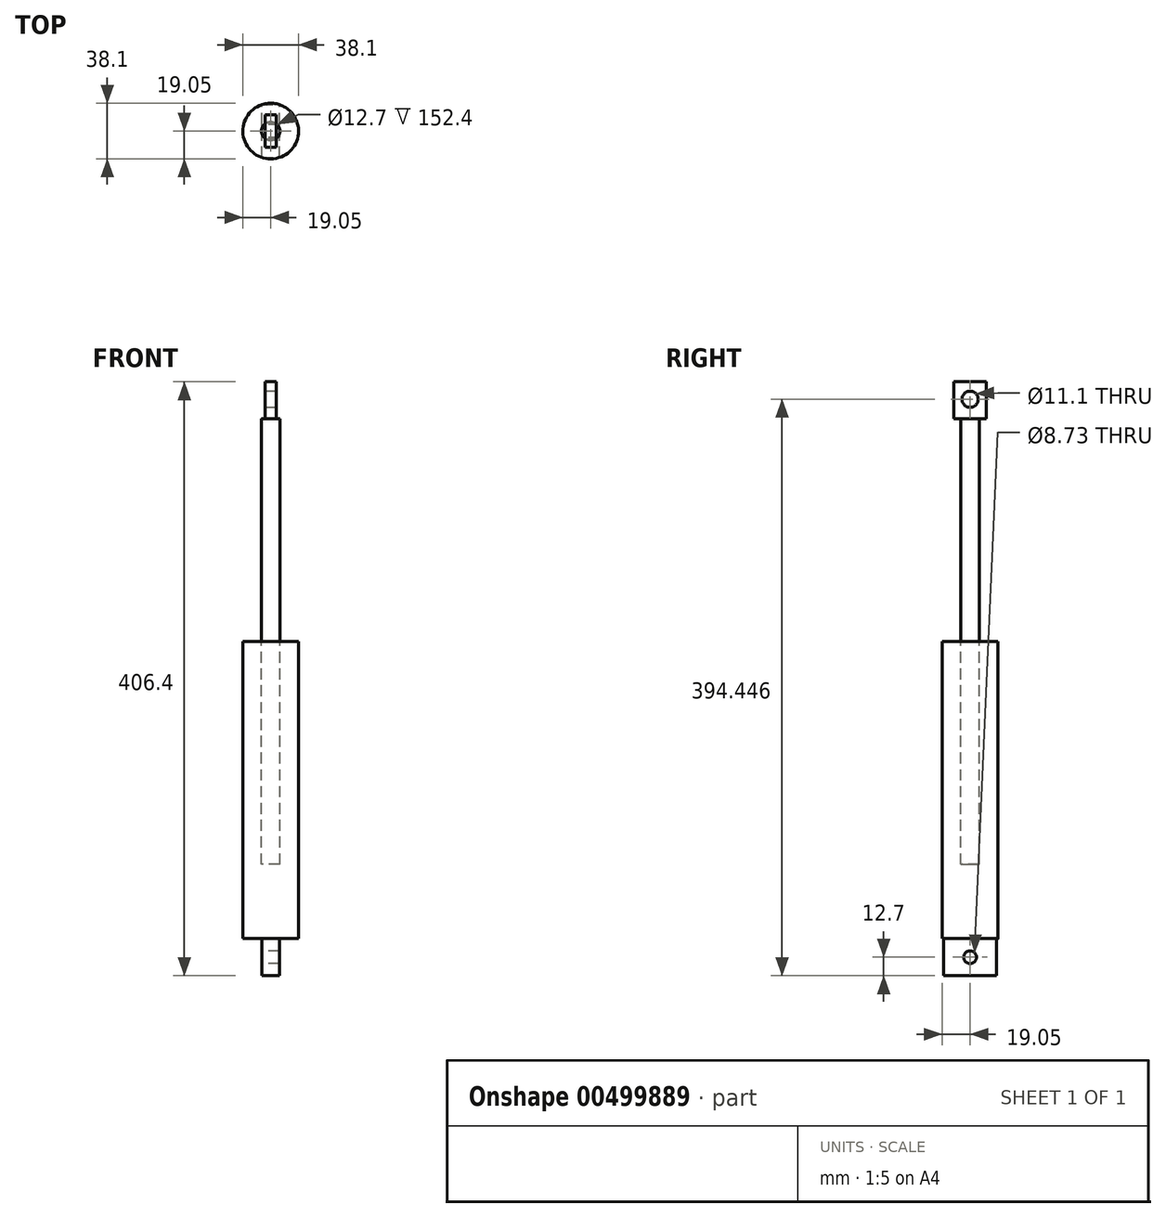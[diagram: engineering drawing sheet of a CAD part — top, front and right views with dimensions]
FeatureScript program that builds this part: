
annotation { "Feature Type Name" : "Feature", "Feature Type Description" : "" }
export const myFeature = defineFeature(function(context is Context, id is Id, definition is map)
    precondition{}
    {
        {
            var Q0;
            Q0=qCreatedBy(makeId("Top.planeOp"),FACE);
            var sketch = newSketch(context, id + "F0", { "sketchPlane" : qUnion([Q0])});
            skCircle(sketch, "E0", {"center": v(0, 0) * mm, "radius": 19.05 * mm});
            skSolve(sketch);
        }
        {
            var Q0;
            Q0=qSketchRegion(id+"F0",true);
            extrude(context, id + "F1", {"entities" : qUnion([Q0]), "depth" : 203.2 * mm});
        }
        {
            var Q0;
            Q0=makeQuery(id+"F1.opExtrude","CAP_FACE",FACE,{"disambiguationData":[OSD([sQuery(id+"F0.wireOp",EDGE,"E0")])],"isStart":false});
            var sketch = newSketch(context, id + "F2", { "sketchPlane" : qUnion([Q0])});
            skCircle(sketch, "E1", {"center": v(0, 0) * mm, "radius": 6.35 * mm});
            skSolve(sketch);
        }
        {
            var Q0;
            Q0=qSketchRegion(id+"F2",true);
            extrude(context, id + "F3", {"entities" : qUnion([Q0]), "operationType" : NewBodyOperationType.REMOVE, "oppositeDirection" : true, "depth" : 152.4 * mm});
        }
        {
            var Q0;
            Q0=makeQuery(id+"F1.opExtrude","CAP_FACE",FACE,{"disambiguationData":[OSD([sQuery(id+"F0.wireOp",EDGE,"E0")])],"isStart":false});
            var sketch = newSketch(context, id + "F4", { "sketchPlane" : qUnion([Q0])});
            skCircle(sketch, "E2.0", {"center": v(0, 0) * mm, "radius": 6.35 * mm});
            skSolve(sketch);
        }
        {
            var Q0;
            Q0=qSketchRegion(id+"F4",true);
            extrude(context, id + "F5", {"entities" : qUnion([Q0]), "depth" : 152.4 * mm});
        }
        {
            var Q0;
            Q0=makeQuery(id+"F5.opExtrude","CAP_FACE",FACE,{"disambiguationData":[OSD([sQuery(id+"F4.wireOp",EDGE,"E2.0")])],"isStart":false});
            var sketch = newSketch(context, id + "F6", { "sketchPlane" : qUnion([Q0])});
            skLineSegment(sketch, "E3.bottom", {"start": v(-3.86, -11.02) * mm, "end": v(3.86, -11.02) * mm});
            skLineSegment(sketch, "E3.top", {"start": v(-3.86, 11.02) * mm, "end": v(3.86, 11.02) * mm});
            skLineSegment(sketch, "E3.left", {"start": v(-3.86, -11.02) * mm, "end": v(-3.86, 11.02) * mm});
            skLineSegment(sketch, "E3.right", {"start": v(3.86, -11.02) * mm, "end": v(3.86, 11.02) * mm});
            skPoint(sketch, "E3.middle", {"position": v(0, 0) * mm});
            skSolve(sketch);
        }
        {
            var Q0;
            Q0=qSketchRegion(id+"F6",true);
            extrude(context, id + "F7", {"entities" : qUnion([Q0]), "operationType" : NewBodyOperationType.ADD, "depth" : 25.4 * mm});
        }
        {
            var Q0;
            Q0=makeQuery(id+"F7.opExtrude","SWEPT_FACE",FACE,{"disambiguationData":[OSD([sQuery(id+"F6.wireOp",EDGE,"E3.left")])]});
            var sketch = newSketch(context, id + "F8", { "sketchPlane" : qUnion([Q0])});
            skCircle(sketch, "E4", {"center": v(0, 369.05) * mm, "radius": 5.55 * mm});
            skSolve(sketch);
        }
        {
            var Q0;
            Q0=qSketchRegion(id+"F8",true);
            extrude(context, id + "F9", {"entities" : qUnion([Q0]), "operationType" : NewBodyOperationType.REMOVE, "oppositeDirection" : true, "depth" : 25.4 * mm});
        }
        {
            var Q0;
            Q0=makeQuery(id+"F1.opExtrude","CAP_FACE",FACE,{"disambiguationData":[OSD([sQuery(id+"F0.wireOp",EDGE,"E0")])],"isStart":true});
            var sketch = newSketch(context, id + "F10", { "sketchPlane" : qUnion([Q0])});
            skLineSegment(sketch, "E5.bottom", {"start": v(-5.93, 18.1) * mm, "end": v(5.93, 18.1) * mm});
            skLineSegment(sketch, "E5.top", {"start": v(-5.93, -18.1) * mm, "end": v(5.93, -18.1) * mm});
            skLineSegment(sketch, "E5.left", {"start": v(-5.93, 18.1) * mm, "end": v(-5.93, -18.1) * mm});
            skLineSegment(sketch, "E5.right", {"start": v(5.93, 18.1) * mm, "end": v(5.93, -18.1) * mm});
            skPoint(sketch, "E5.middle", {"position": v(0, 0) * mm});
            skSolve(sketch);
        }
        {
            var Q0;
            Q0=qSketchRegion(id+"F10",true);
            extrude(context, id + "F11", {"entities" : qUnion([Q0]), "operationType" : NewBodyOperationType.ADD, "depth" : 25.4 * mm});
        }
        {
            var Q0;
            Q0=makeQuery(id+"F11.opExtrude","SWEPT_FACE",FACE,{"disambiguationData":[OSD([sQuery(id+"F10.wireOp",EDGE,"E5.left")])]});
            var sketch = newSketch(context, id + "F12", { "sketchPlane" : qUnion([Q0])});
            skCircle(sketch, "E6", {"center": v(0, -12.7) * mm, "radius": 4.36 * mm});
            skSolve(sketch);
        }
        {
            var Q0;
            Q0=qSketchRegion(id+"F12",true);
            extrude(context, id + "F13", {"entities" : qUnion([Q0]), "operationType" : NewBodyOperationType.REMOVE, "oppositeDirection" : true, "depth" : 25.4 * mm});
        }
    });
